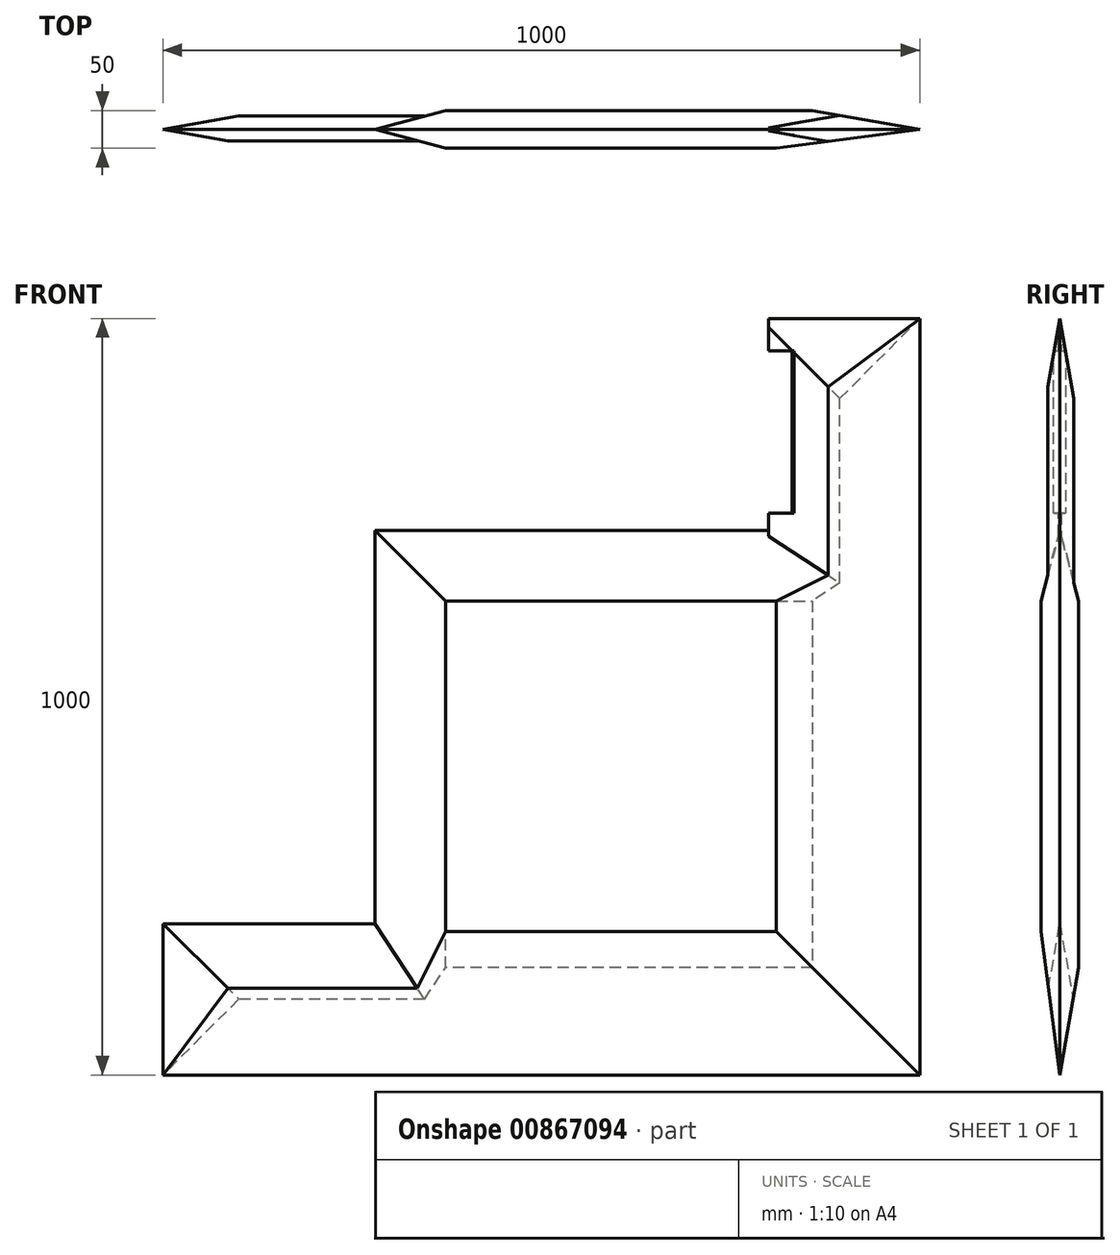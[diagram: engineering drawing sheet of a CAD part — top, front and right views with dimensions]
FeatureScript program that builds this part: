
annotation { "Feature Type Name" : "Feature", "Feature Type Description" : "" }
export const myFeature = defineFeature(function(context is Context, id is Id, definition is map)
    precondition{}
    {
        {
            var Q0;
            Q0=qCreatedBy(makeId("Front.planeOp"),FACE);
            var sketch = newSketch(context, id + "F0", { "sketchPlane" : qUnion([Q0])});
            skLineSegment(sketch, "E0", {"start": v(0, 0) * mm, "end": v(1000, 0) * mm});
            skLineSegment(sketch, "E1", {"start": v(1000, 0) * mm, "end": v(1000, 1000) * mm});
            skLineSegment(sketch, "E2", {"start": v(1000, 1000) * mm, "end": v(800, 1000) * mm});
            skLineSegment(sketch, "E3", {"start": v(0, 0) * mm, "end": v(0, 200) * mm});
            skLineSegment(sketch, "E4", {"start": v(800, 1000) * mm, "end": v(800, 720) * mm});
            skLineSegment(sketch, "E5", {"start": v(0, 200) * mm, "end": v(280, 200) * mm});
            skLineSegment(sketch, "E6", {"start": v(280, 720) * mm, "end": v(280, 200) * mm});
            skLineSegment(sketch, "E7", {"start": v(280, 720) * mm, "end": v(800, 720) * mm});
            skPoint(sketch, "E8.trimOffspring.end.orphan", {"position": v(0, 1000) * mm});
            skPoint(sketch, "E9.end.orphan", {"position": v(280, 460) * mm});
            skPoint(sketch, "E10.start.orphan", {"position": v(540, 720) * mm});
            skPoint(sketch, "E11.start.orphan", {"position": v(800, 200) * mm});
            skSolve(sketch);
        }
        {
            var Q0;
            Q0=makeQuery(id+"F0.imprint","IMPRINT",FACE,{"disambiguationData":[TD([[makeQuery(id+"F0.imprint","IMPRINT",EDGE,{"derivedFrom":sQuery(id+"F0.wireOp",EDGE,"E0")}),1.0]])]});
            extrude(context, id + "F1", {"entities" : qUnion([Q0]), "depth" : 50 * mm, "offsetDistance" : 25 * mm});
        }
        {
            var Q0;
            Q0=makeQuery(id+"F1.opExtrude","SWEPT_BODY",BODY,{"disambiguationData":[OSD([sQuery(id+"F0.wireOp",EDGE,"E0"),sQuery(id+"F0.wireOp",EDGE,"E1"),sQuery(id+"F0.wireOp",EDGE,"E2"),sQuery(id+"F0.wireOp",EDGE,"E3"),sQuery(id+"F0.wireOp",EDGE,"E4"),sQuery(id+"F0.wireOp",EDGE,"E5"),sQuery(id+"F0.wireOp",EDGE,"E6"),sQuery(id+"F0.wireOp",EDGE,"E7")])]});
            transform(context, id + "F2", {"entities" : qUnion([Q0]), "transformType" : TransformType.TRANSLATION_3D, "dx" : 1592 * mm, "dy" : 0 * mm, "dz" : 0 * mm, "makeCopy" : false});
        }
        {
            var Q0;
            Q0=makeQuery(id+"F1.opExtrude","CAP_EDGE",EDGE,{"disambiguationData":[OSD([sQuery(id+"F0.wireOp",EDGE,"E1")])],"isStart":true});
            var Q1;
            Q1=makeQuery(id+"F1.opExtrude","CAP_EDGE",EDGE,{"disambiguationData":[OSD([sQuery(id+"F0.wireOp",EDGE,"E0")])],"isStart":true});
            chamfer(context, id + "F3", {"entities" : qUnion([Q0, Q1]), "chamferType" : ChamferType.OFFSET_ANGLE, "width" : 25 * mm, "oppositeDirection" : false, "angle" : 80 * degree, "tangentPropagation" : true});
        }
        {
            var Q0;
            Q0=makeQuery(id+"F1.opExtrude","CAP_EDGE",EDGE,{"disambiguationData":[OSD([sQuery(id+"F0.wireOp",EDGE,"E0")])],"isStart":false});
            var Q1;
            Q1=makeQuery(id+"F1.opExtrude","CAP_EDGE",EDGE,{"disambiguationData":[OSD([sQuery(id+"F0.wireOp",EDGE,"E1")])],"isStart":false});
            chamfer(context, id + "F4", {"entities" : qUnion([Q0, Q1]), "chamferType" : ChamferType.OFFSET_ANGLE, "width" : 25 * mm, "oppositeDirection" : true, "angle" : 82.5 * degree, "tangentPropagation" : true});
        }
        {
            var Q0;
            Q0=makeQuery(id+"F1.opExtrude","CAP_EDGE",EDGE,{"disambiguationData":[OSD([sQuery(id+"F0.wireOp",EDGE,"E2")])],"isStart":true});
            var Q1;
            Q1=makeQuery(id+"F1.opExtrude","CAP_EDGE",EDGE,{"disambiguationData":[OSD([sQuery(id+"F0.wireOp",EDGE,"E2")])],"isStart":false});
            var Q2;
            Q2=makeQuery(id+"F1.opExtrude","CAP_EDGE",EDGE,{"disambiguationData":[OSD([sQuery(id+"F0.wireOp",EDGE,"E3")])],"isStart":true});
            var Q3;
            Q3=makeQuery(id+"F1.opExtrude","CAP_EDGE",EDGE,{"disambiguationData":[OSD([sQuery(id+"F0.wireOp",EDGE,"E3")])],"isStart":false});
            chamfer(context, id + "F5", {"entities" : qUnion([Q0, Q1, Q2, Q3]), "chamferType" : ChamferType.OFFSET_ANGLE, "width" : 25 * mm, "oppositeDirection" : false, "angle" : 80 * degree, "tangentPropagation" : true});
        }
        {
            var Q0;
            Q0=makeQuery(id+"F1.opExtrude","CAP_EDGE",EDGE,{"disambiguationData":[OSD([sQuery(id+"F0.wireOp",EDGE,"E4")])],"isStart":false});
            var Q1;
            Q1=makeQuery(id+"F1.opExtrude","CAP_EDGE",EDGE,{"disambiguationData":[OSD([sQuery(id+"F0.wireOp",EDGE,"E4")])],"isStart":true});
            chamfer(context, id + "F6", {"entities" : qUnion([Q0, Q1]), "chamferType" : ChamferType.OFFSET_ANGLE, "width" : 23 * mm, "oppositeDirection" : true, "angle" : 80 * degree, "tangentPropagation" : true});
        }
        {
            var Q0;
            Q0=makeQuery(id+"F1.opExtrude","CAP_EDGE",EDGE,{"disambiguationData":[OSD([sQuery(id+"F0.wireOp",EDGE,"E5")])],"isStart":true});
            var Q1;
            Q1=makeQuery(id+"F1.opExtrude","CAP_EDGE",EDGE,{"disambiguationData":[OSD([sQuery(id+"F0.wireOp",EDGE,"E5")])],"isStart":false});
            chamfer(context, id + "F7", {"entities" : qUnion([Q0, Q1]), "chamferType" : ChamferType.OFFSET_ANGLE, "width" : 25 * mm, "oppositeDirection" : true, "angle" : 80 * degree, "tangentPropagation" : true});
        }
        {
            var Q0;
            Q0=makeQuery(id+"F1.opExtrude","CAP_EDGE",EDGE,{"disambiguationData":[OSD([sQuery(id+"F0.wireOp",EDGE,"E6")])],"isStart":true});
            var Q1;
            Q1=makeQuery(id+"F1.opExtrude","CAP_EDGE",EDGE,{"disambiguationData":[OSD([sQuery(id+"F0.wireOp",EDGE,"E6")])],"isStart":false});
            var Q2;
            Q2=makeQuery(id+"F1.opExtrude","CAP_EDGE",EDGE,{"disambiguationData":[OSD([sQuery(id+"F0.wireOp",EDGE,"E7")])],"isStart":false});
            var Q3;
            Q3=makeQuery(id+"F1.opExtrude","CAP_EDGE",EDGE,{"disambiguationData":[OSD([sQuery(id+"F0.wireOp",EDGE,"E7")])],"isStart":true});
            chamfer(context, id + "F8", {"entities" : qUnion([Q0, Q1, Q2, Q3]), "chamferType" : ChamferType.OFFSET_ANGLE, "width" : 25 * mm, "oppositeDirection" : false, "angle" : 75 * degree, "tangentPropagation" : true});
        }
        {
            var Q0;
            {var subQ0=sQuery(id+"F0.wireOp",EDGE,"E4");Q0=makeQuery(id+"F6.opChamfer","BLEND_FACE",FACE,{"disambiguationData":[OSD([subQ0]),TDD([makeQuery(id+"F1.opExtrude","CAP_EDGE",EDGE,{"disambiguationData":[OSD([subQ0])],"isStart":true})])]});}
            var sketch = newSketch(context, id + "F9", { "sketchPlane" : qUnion([Q0])});
            skLineSegment(sketch, "E12", {"start": v(-2347.26, 957.35) * mm, "end": v(-2383.46, 957.35) * mm});
            skLineSegment(sketch, "E13", {"start": v(-2383.46, 957.35) * mm, "end": v(-2383.46, 742.43) * mm});
            skLineSegment(sketch, "E14", {"start": v(-2383.46, 742.43) * mm, "end": v(-2346.7, 742.43) * mm});
            skLineSegment(sketch, "E15", {"start": v(-2347.26, 957.35) * mm, "end": v(-2346.7, 742.43) * mm});
            skSolve(sketch);
        }
        {
            var Q0;
            {var subQ0=sQuery(id+"F9.wireOp",EDGE,"E15");Q0=makeQuery(id+"F9.imprint","IMPRINT",FACE,{"disambiguationData":[TD([[makeQuery(id+"F9.imprint","IMPRINT",EDGE,{"derivedFrom":subQ0}),-1.0]])]});}
            var Q1;
            {var subQ0=sQuery(id+"F9.wireOp",EDGE,"E13");Q1=makeQuery(id+"F9.imprint","IMPRINT",FACE,{"disambiguationData":[TD([[makeQuery(id+"F9.imprint","IMPRINT",EDGE,{"derivedFrom":subQ0}),1.0]])]});}
            extrude(context, id + "F10", {"entities" : qUnion([Q0, Q1]), "operationType" : NewBodyOperationType.REMOVE, "oppositeDirection" : true, "depth" : 25 * mm, "offsetDistance" : 25 * mm});
        }
    });
